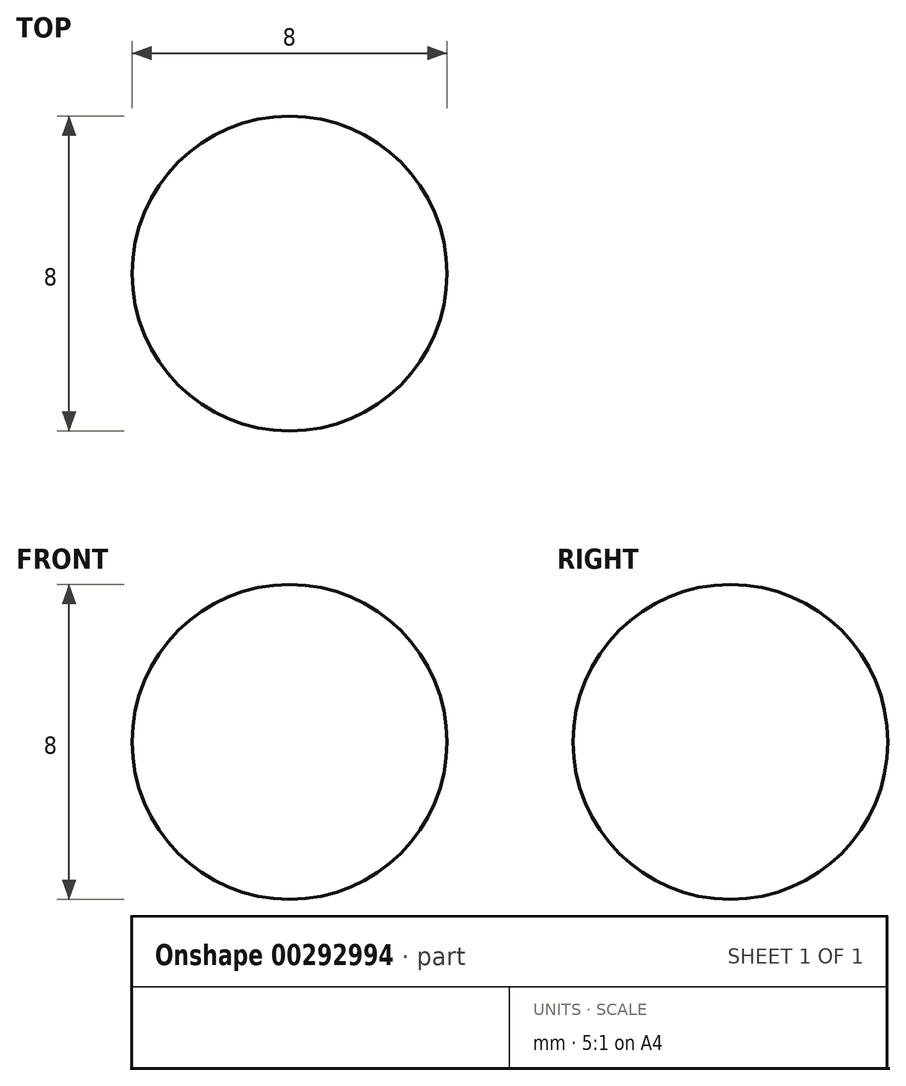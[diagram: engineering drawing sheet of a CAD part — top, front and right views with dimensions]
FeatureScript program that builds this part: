
annotation { "Feature Type Name" : "Feature", "Feature Type Description" : "" }
export const myFeature = defineFeature(function(context is Context, id is Id, definition is map)
    precondition{}
    {
        {
            var Q0;
            Q0=qCreatedBy(makeId("Right.planeOp"),FACE);
            var sketch = newSketch(context, id + "F0", { "sketchPlane" : qUnion([Q0])});
            skLineSegment(sketch, "E0", {"start": v(0, 0) * mm, "end": v(0, 14.5) * mm});
            skSolve(sketch);
        }
        {
            var Q0;
            Q0=qCreatedBy(makeId("Right.planeOp"),FACE);
            var sketch = newSketch(context, id + "F1", { "sketchPlane" : qUnion([Q0])});
            skArc(sketch, "E1", {"start": v(0, 4) * mm, "mid": v(-4, 0) * mm, "end": v(0, -4) * mm});
            skLineSegment(sketch, "E2", {"start": v(0, -4) * mm, "end": v(0, 8.6) * mm});
            skSolve(sketch);
        }
        {
            var Q0;
            {var subQ0=sQuery(id+"F1.wireOp",EDGE,"E1");Q0=makeQuery(id+"F1.imprint","IMPRINT",FACE,{"disambiguationData":[TD([[makeQuery(id+"F1.imprint","IMPRINT",EDGE,{"derivedFrom":subQ0}),1.0]])]});}
            var Q1;
            Q1=sQuery(id+"F0.wireOp",EDGE,"E0");
            revolve(context, id + "F2", {"entities" : qUnion([Q0]), "axis" : qUnion([Q1]), "revolveType" : RevolveType.FULL});
        }
    });
